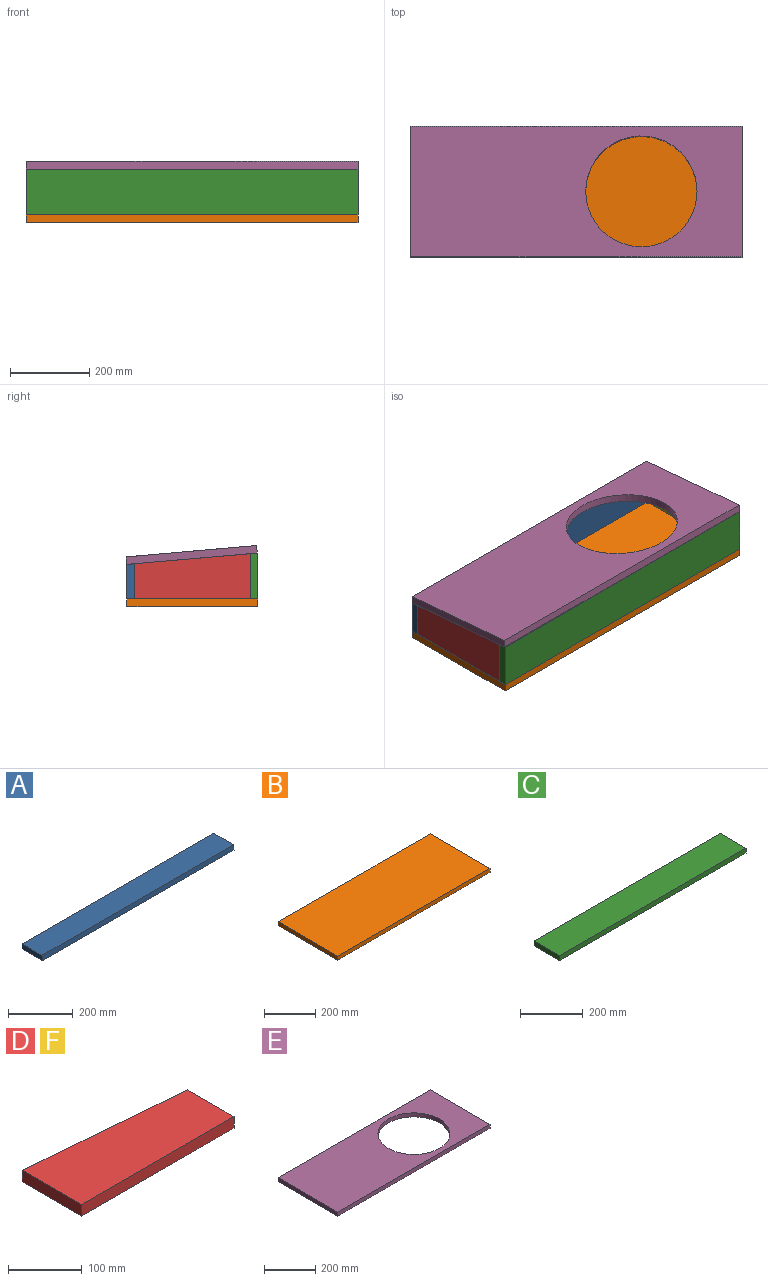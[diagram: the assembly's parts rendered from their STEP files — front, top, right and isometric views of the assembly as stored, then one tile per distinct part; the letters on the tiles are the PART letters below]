
ASSEMBLY  parts=6 mates=5
PART A: 6 faces, bbox 838.2x88.9x19.1 mm
  f0: plane 88.9x19.05mm, normal (-1,0,0), area 1677.7mm2, adj f2,f3,f4,f5
  f1: plane 88.9x19.05mm, normal (1,0,0), area 1677.7mm2, adj f2,f3,f4,f5
  f2: plane 838.2x19.05mm, normal (0,1,0), area 15967.7mm2, adj f0,f1,f3,f4
  f3: plane 838.2x87.23mm, normal (0,0,1), area 73119mm2, adj f0,f1,f2,f5
  f4: plane 838.2x88.9mm, normal (0,0,-1), area 74516mm2, adj f0,f1,f2,f5
  f5: plane 838.2x19.05mm, normal (0,-1,0.09), area 16028.7mm2, adj f0,f1,f3,f4
PART B: 6 faces, bbox 838.2x330.2x19.1 mm
  f0: plane 330.2x19.05mm, normal (-1,0,0), area 6290.3mm2, adj f1,f3,f4,f5
  f1: plane 838.2x19.05mm, normal (0,-1,0), area 15967.7mm2, adj f0,f2,f4,f5
  f2: plane 330.2x19.05mm, normal (1,0,0), area 6290.3mm2, adj f1,f3,f4,f5
  f3: plane 838.2x19.05mm, normal (0,1,0), area 15967.7mm2, adj f0,f2,f4,f5
  f4: plane 838.2x330.2mm, normal (0,0,1), area 276773.6mm2, adj f0,f1,f2,f3
  f5: plane 838.2x330.2mm, normal (0,0,-1), area 276773.6mm2, adj f0,f1,f2,f3
PART C: 6 faces, bbox 838.2x115.6x19.1 mm
  f0: plane 115.57x19.05mm, normal (-1,0,0), area 2188.9mm2, adj f1,f3,f4,f5
  f1: plane 838.2x114.24mm, normal (0,0,-1), area 95754.2mm2, adj f0,f2,f3,f5
  f2: plane 115.57x19.05mm, normal (1,0,0), area 2188.9mm2, adj f1,f3,f4,f5
  f3: plane 838.2x19.05mm, normal (0,-1,0), area 15967.7mm2, adj f0,f1,f2,f4
  f4: plane 838.2x115.57mm, normal (0,0,1), area 96870.8mm2, adj f0,f2,f3,f5
  f5: plane 838.2x19.05mm, normal (0,1,-0.07), area 16006.7mm2, adj f0,f1,f2,f4
PART D: 6 faces, bbox 292.1x114.3x19.1 mm
  f0: plane 114.3x19.05mm, normal (-1,0,0), area 2177.4mm2, adj f1,f3,f4,f5
  f1: plane 292.1x19.05mm, normal (0,-1,0), area 5564.5mm2, adj f0,f2,f3,f4
  f2: plane 88.9x19.05mm, normal (1,0,0), area 1693.5mm2, adj f1,f3,f4,f5
  f3: plane 292.1x114.3mm, normal (0,0,1), area 29677.4mm2, adj f0,f1,f2,f5
  f4: plane 292.1x114.3mm, normal (0,0,-1), area 29677.4mm2, adj f0,f1,f2,f5
  f5: plane 292.1x25.4mm, normal (0.09,1,0), area 5585.5mm2, adj f0,f2,f3,f4
PART E: 7 faces, bbox 838.2x330.2x19.1 mm
  f0: plane 330.2x19.05mm, normal (-1,0,0), area 6290.3mm2, adj f1,f3,f4,f5
  f1: plane 838.2x19.05mm, normal (0,-1,0), area 15967.7mm2, adj f0,f2,f4,f5
  f2: plane 330.2x19.05mm, normal (1,0,0), area 6290.3mm2, adj f1,f3,f4,f5
  f3: plane 838.2x19.05mm, normal (0,1,0), area 15967.7mm2, adj f0,f2,f4,f5
  f4: plane 838.2x330.2mm, normal (0,0,1), area 214791.4mm2, adj f0,f1,f2,f3,f6
  f5: plane 838.2x330.2mm, normal (0,0,-1), area 214791.4mm2, adj f0,f1,f2,f3,f6
  f6: cylinder r=140.46mm len=280.92mm, axis (0,0,1), area 16812.6mm2, adj f4,f5
PART F: same geometry as D
PLACE A rot(axis=(-1,0,0),90deg) t=(-26.46,358.29,76.74)mm
PLACE B t=(-26.46,47.14,-31.21)mm fixed
PLACE C rot(axis=(1,0,0),90deg) t=(-26.46,66.19,-12.16)mm
PLACE D rot(axis=(0.58,0.58,0.58),120deg) t=(-26.46,66.19,-12.16)mm
PLACE E rot(axis=(-1,0,0),5deg) t=(-26.46,48.4,103.86)mm
PLACE F rot(axis=(0.58,0.58,0.58),120deg) t=(792.69,66.19,-12.16)mm
MATE fastened E.f5 <-> A.f5  axis (0,-0.09,-1) through (811.74,377.34,75.08)mm
MATE fastened F.f0 <-> C.f1  axis (0,-1,0) through (811.74,66.19,-12.16)mm
MATE fastened A.f2 <-> B.f4  axis (0,0,-1) through (811.74,377.34,-12.16)mm
MATE fastened D.f0 <-> C.f1  axis (0,-1,0) through (-26.46,66.19,-12.16)mm
MATE fastened C.f3 <-> B.f4  axis (0,0,-1) through (-26.46,47.14,-12.16)mm
